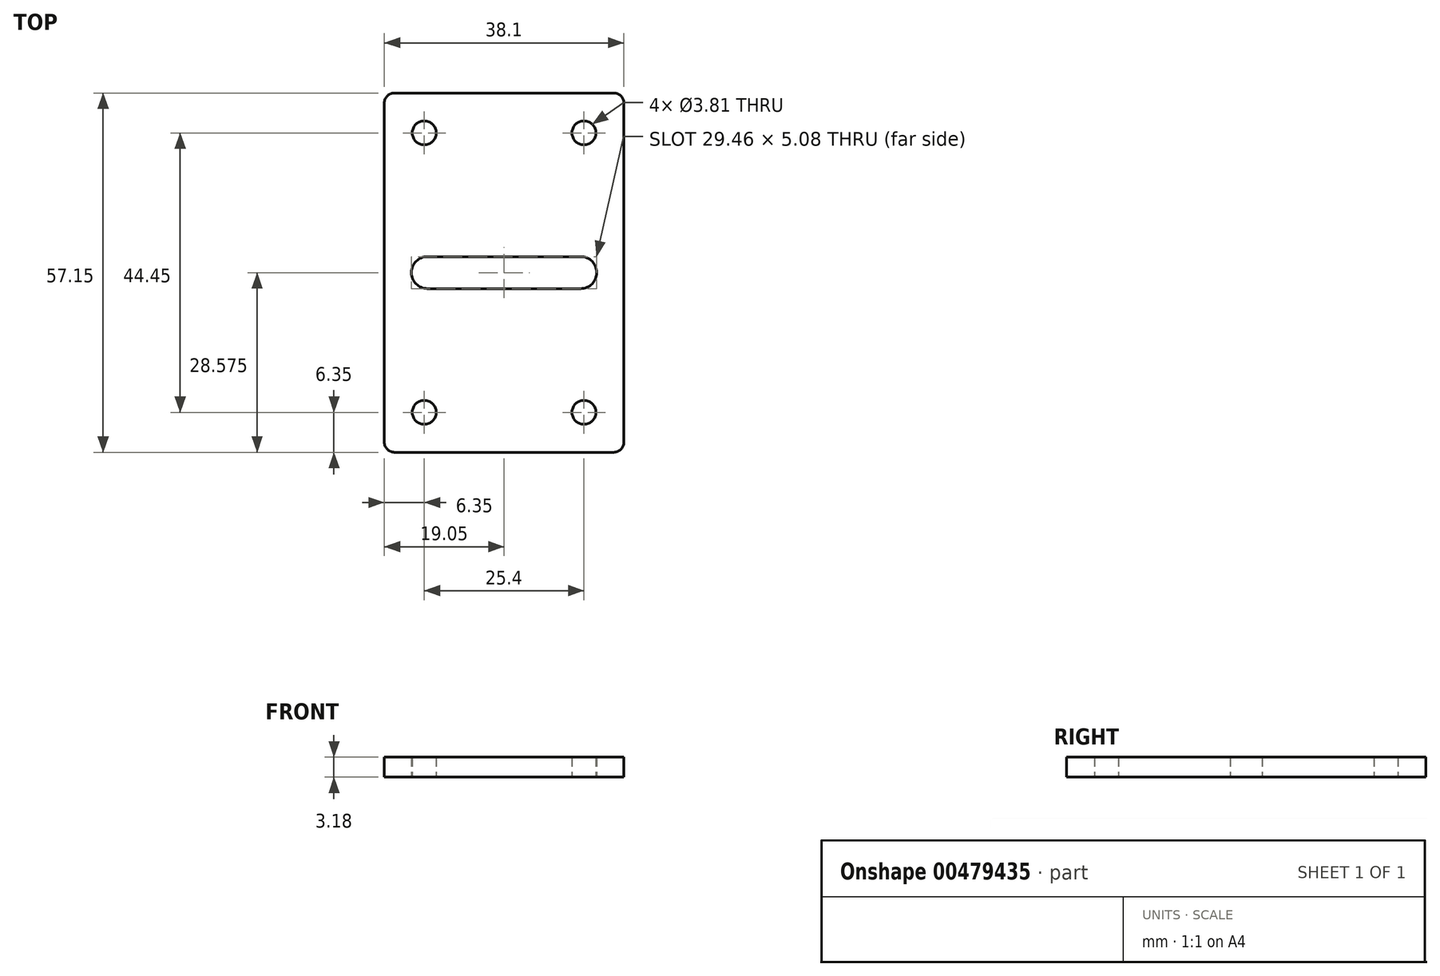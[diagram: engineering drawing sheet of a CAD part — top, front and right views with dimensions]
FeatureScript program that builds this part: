
annotation { "Feature Type Name" : "Feature", "Feature Type Description" : "" }
export const myFeature = defineFeature(function(context is Context, id is Id, definition is map)
    precondition{}
    {
        {
            var Q0;
            Q0=qCreatedBy(makeId("Top.planeOp"),FACE);
            var sketch = newSketch(context, id + "F0", { "sketchPlane" : qUnion([Q0])});
            skLineSegment(sketch, "E0.bottom", {"start": v(1.6, 0) * mm, "end": v(36.5, 0) * mm});
            skLineSegment(sketch, "E0.top", {"start": v(1.6, 57.15) * mm, "end": v(36.5, 57.15) * mm});
            skLineSegment(sketch, "E0.left", {"start": v(0, 1.6) * mm, "end": v(0, 55.55) * mm});
            skLineSegment(sketch, "E0.right", {"start": v(38.1, 1.6) * mm, "end": v(38.1, 55.55) * mm});
            skCircle(sketch, "E1", {"center": v(6.35, 50.8) * mm, "radius": 1.9 * mm});
            skCircle(sketch, "E2", {"center": v(31.75, 50.8) * mm, "radius": 1.9 * mm});
            skCircle(sketch, "E3", {"center": v(6.86, 28.58) * mm, "radius": 2.54 * mm});
            skCircle(sketch, "E4", {"center": v(31.24, 28.58) * mm, "radius": 2.54 * mm});
            skCircle(sketch, "E5", {"center": v(6.35, 6.35) * mm, "radius": 1.9 * mm});
            skCircle(sketch, "E6", {"center": v(31.75, 6.35) * mm, "radius": 1.9 * mm});
            skLineSegment(sketch, "E7.bottom", {"start": v(6.86, 31.12) * mm, "end": v(31.24, 31.12) * mm});
            skLineSegment(sketch, "E7.top", {"start": v(6.86, 26.04) * mm, "end": v(31.24, 26.04) * mm});
            skLineSegment(sketch, "E7.left", {"start": v(6.86, 31.12) * mm, "end": v(6.86, 26.04) * mm});
            skLineSegment(sketch, "E7.right", {"start": v(31.24, 31.12) * mm, "end": v(31.24, 26.04) * mm});
            skPoint(sketch, "E8.visualSharp", {"position": v(0, 57.15) * mm});
            skArc(sketch, "E8.filletArc", {"start": v(1.6, 57.15) * mm, "mid": v(0.47, 56.68) * mm, "end": v(0, 55.55) * mm});
            skPoint(sketch, "E9.visualSharp", {"position": v(38.1, 57.15) * mm});
            skArc(sketch, "E9.filletArc", {"start": v(38.1, 55.55) * mm, "mid": v(37.63, 56.68) * mm, "end": v(36.5, 57.15) * mm});
            skPoint(sketch, "E10.visualSharp", {"position": v(38.1, 0) * mm});
            skArc(sketch, "E10.filletArc", {"start": v(36.5, 0) * mm, "mid": v(37.63, 0.47) * mm, "end": v(38.1, 1.6) * mm});
            skPoint(sketch, "E11.visualSharp", {"position": v(0, 0) * mm});
            skArc(sketch, "E11.filletArc", {"start": v(0, 1.6) * mm, "mid": v(0.47, 0.47) * mm, "end": v(1.6, 0) * mm});
            skSolve(sketch);
        }
        {
            var Q0;
            Q0=makeQuery(id+"F0.imprint","IMPRINT",FACE,{"disambiguationData":[TD([[makeQuery(id+"F0.imprint","IMPRINT",EDGE,{"derivedFrom":sQuery(id+"F0.wireOp",EDGE,"E0.bottom")}),1.0]])]});
            extrude(context, id + "F1", {"entities" : qUnion([Q0]), "depth" : 3.17 * mm, "offsetDistance" : 25.4 * mm});
        }
    });
